# Revit family: BLE-W-DBW-LED
name_source: partatom
category: Lighting Fixtures
units: mm (PartAtom-declared; Revit-internal decimal feet)

## family parameters
Cut with Voids When Loaded = No
Host = Face
Light Source = Yes
Maintain Annotation Orientation = No
Part Type = Normal
Room Calculation Point = No
Round Connector Dimension = Use Diameter
Shared = No

## types (6) — shared parameters
Base Material = 100 - Black
Color Filter = 16777215
Default Elevation = 4' - 0"
Dimming Lamp Color Temperature Shift = <None>
Emit from Line Length = 2' - 0"
Nut Material = 100 - Black
Photometric Web File = generic
Shade Material = 100 - Black
Tilt Angle = 0.00°

## per-type parameters (varying)
| type | 12" | 14" | 16" | Dome | Flat | Heat Sink | Heat Sink 6" | Heat Sink 9" | Light Source Distance |
| 12" Dome | Yes | No | No | Yes | No | 0' - 4 3/4" | Yes | No | 0' - 4 13/16" |
| 14" Dome | No | Yes | No | Yes | No | 0' - 6 3/32" | No | Yes | 0' - 6 5/32" |
| 16" Dome | No | No | Yes | Yes | No | 0' - 5 13/16" | No | Yes | 0' - 5 7/8" |
| 12" Flat | Yes | No | No | No | Yes | 0' - 4 3/4" | Yes | No | 0' - 4 13/16" |
| 14" Flat | No | Yes | No | No | Yes | 0' - 6 3/32" | No | Yes | 0' - 6 5/32" |
| 16" Flat | No | No | Yes | No | Yes | 0' - 5 13/16" | No | Yes | 0' - 5 7/8" |

## geometry (parser evidence)
native form markers: Sweep x56
no freeform markers — native parametric forms only
